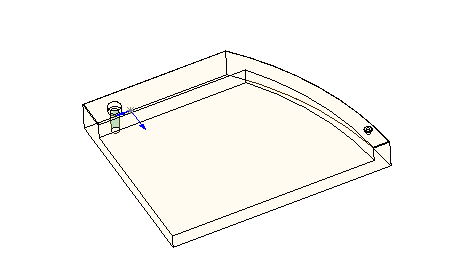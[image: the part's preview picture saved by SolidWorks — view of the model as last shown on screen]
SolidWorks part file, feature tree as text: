
SOLIDWORKS PART (.sldprt)
format: sldprt  version: not decoded by parser v0  size: 212,992 bytes
history: native  units: mm
features: cut_extrude x4, plane x2, extrude x2, sketch x1, fillet x1 + 10 further entries (+7 scaffold rows collapsed)
feature tree (27):
  scaffold x7  (default folders/planes/origin — collapsed)
  "Corps de surface"
  plane  "Face"
  "Dessus"
  "Droite"
  sketch  "Esquisse1"
  "param"
  plane  "gss_2demu_pline1"
  "param"
  extrude  "Extrusion2"  Depth=95mm
  "Esquisse2"
  "Esquisse3"
  cut_extrude  "Enlèv. mat.-Extru.2"  Depth=20mm
  extrude  "Extrusion3"  Depth=3mm
  "Esquisse5"
  cut_extrude  "Enlèv. mat.-Extru.4"  Depth=18.5mm
  fillet  "Congé1"  Radius=2mm
  "Esquisse6"
  cut_extrude  "Enlèv. mat.-Extru.5"  [1 undecoded]
  "Esquisse7"
  cut_extrude  "Enlèv. mat.-Extru.13"  Depth=50mm
decode coverage: 6 of 8 modeling features carry decoded parameters; 10 rows unclassified (native names shown)
note: 1 parameter value undecoded
note: suppression state not decoded; provenance and decode notes live in map.json
